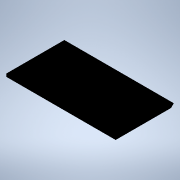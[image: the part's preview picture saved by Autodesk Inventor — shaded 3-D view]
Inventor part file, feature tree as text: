
AUTODESK INVENTOR PART (.ipt)
format: ipt  version: 2022 (Build 260153000, 153)  size: 103,424 bytes
history: native  units: mm
features: other x1, extrude x1, chamfer x1, sketch x1
ambient origin geometry x8: Origin, YZ Plane, XZ Plane, XY Plane, X Axis, Y Axis, Z Axis, Center Point
bodies: Body1 (feature_tree)
feature tree (4):
  other  "ソリッド1"
  extrude  "押し出し1"  Depth=80.0mm
  chamfer  "面取り4"  Distance=42.5mm
  sketch  "スケッチ1"
